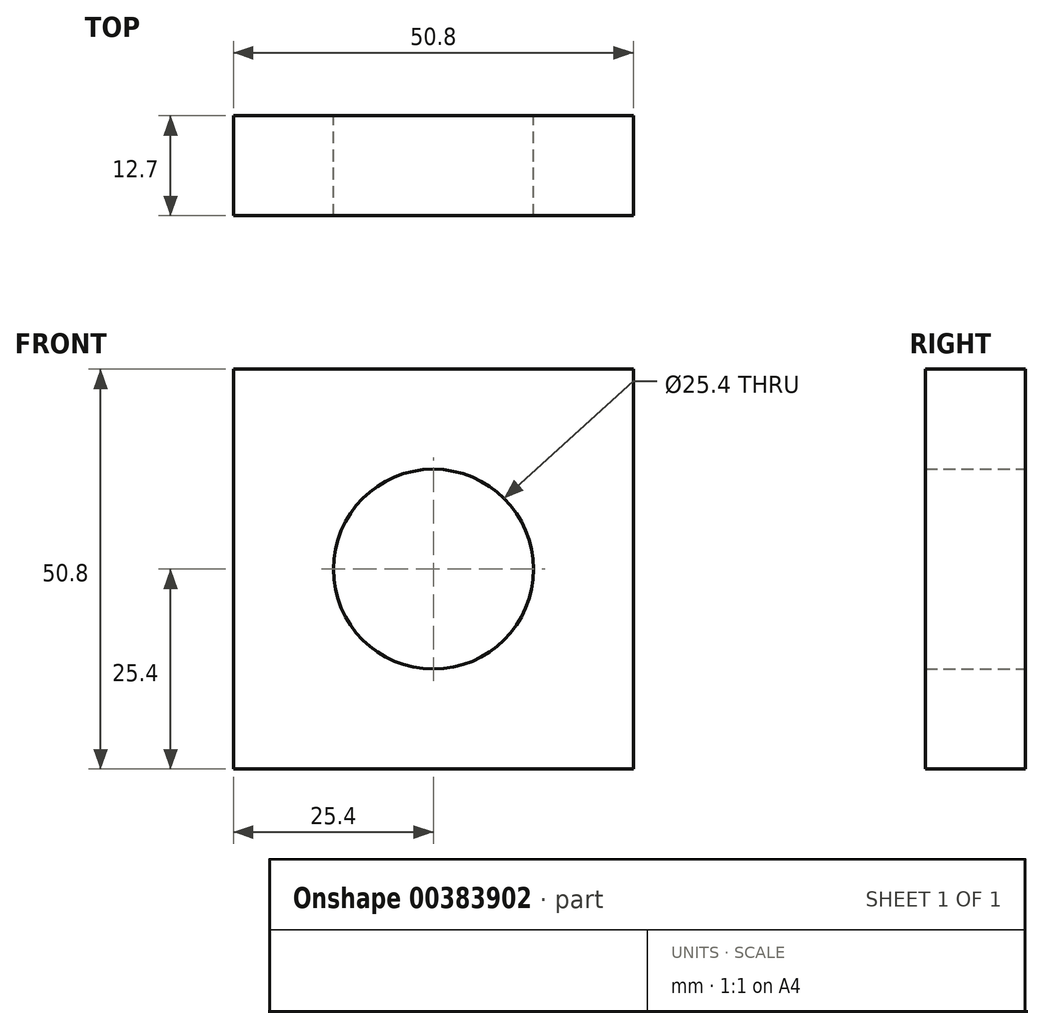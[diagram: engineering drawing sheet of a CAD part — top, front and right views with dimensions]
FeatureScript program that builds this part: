
annotation { "Feature Type Name" : "Feature", "Feature Type Description" : "" }
export const myFeature = defineFeature(function(context is Context, id is Id, definition is map)
    precondition{}
    {
        {
            var Q0;
            Q0=qCreatedBy(makeId("Front.planeOp"),FACE);
            var sketch = newSketch(context, id + "F0", { "sketchPlane" : qUnion([Q0])});
            skLineSegment(sketch, "E0.bottom", {"start": v(25.4, 25.4) * mm, "end": v(-25.4, 25.4) * mm});
            skLineSegment(sketch, "E0.top", {"start": v(25.4, -25.4) * mm, "end": v(-25.4, -25.4) * mm});
            skLineSegment(sketch, "E0.left", {"start": v(25.4, 25.4) * mm, "end": v(25.4, -25.4) * mm});
            skLineSegment(sketch, "E0.right", {"start": v(-25.4, 25.4) * mm, "end": v(-25.4, -25.4) * mm});
            skPoint(sketch, "E0.middle", {"position": v(0, 0) * mm});
            skSolve(sketch);
        }
        {
            var Q0;
            Q0 = qSketchRegion(id + "F0", true);
            extrude(context, id + "F1", {"entities" : qUnion([Q0]), "depth" : 12.7 * mm});
        }
        {
            var Q0;
            Q0=qCreatedBy(makeId("Front.planeOp"),FACE);
            var sketch = newSketch(context, id + "F2", { "sketchPlane" : qUnion([Q0])});
            skCircle(sketch, "E1", {"center": v(0, 0) * mm, "radius": 12.7 * mm});
            skSolve(sketch);
        }
        {
            var Q0;
            Q0 = qSketchRegion(id + "F2", true);
            extrude(context, id + "F3", {"entities" : qUnion([Q0]), "operationType" : NewBodyOperationType.REMOVE, "endBound" : BoundingType.THROUGH_ALL, "depth" : 25.4 * mm});
        }
    });
